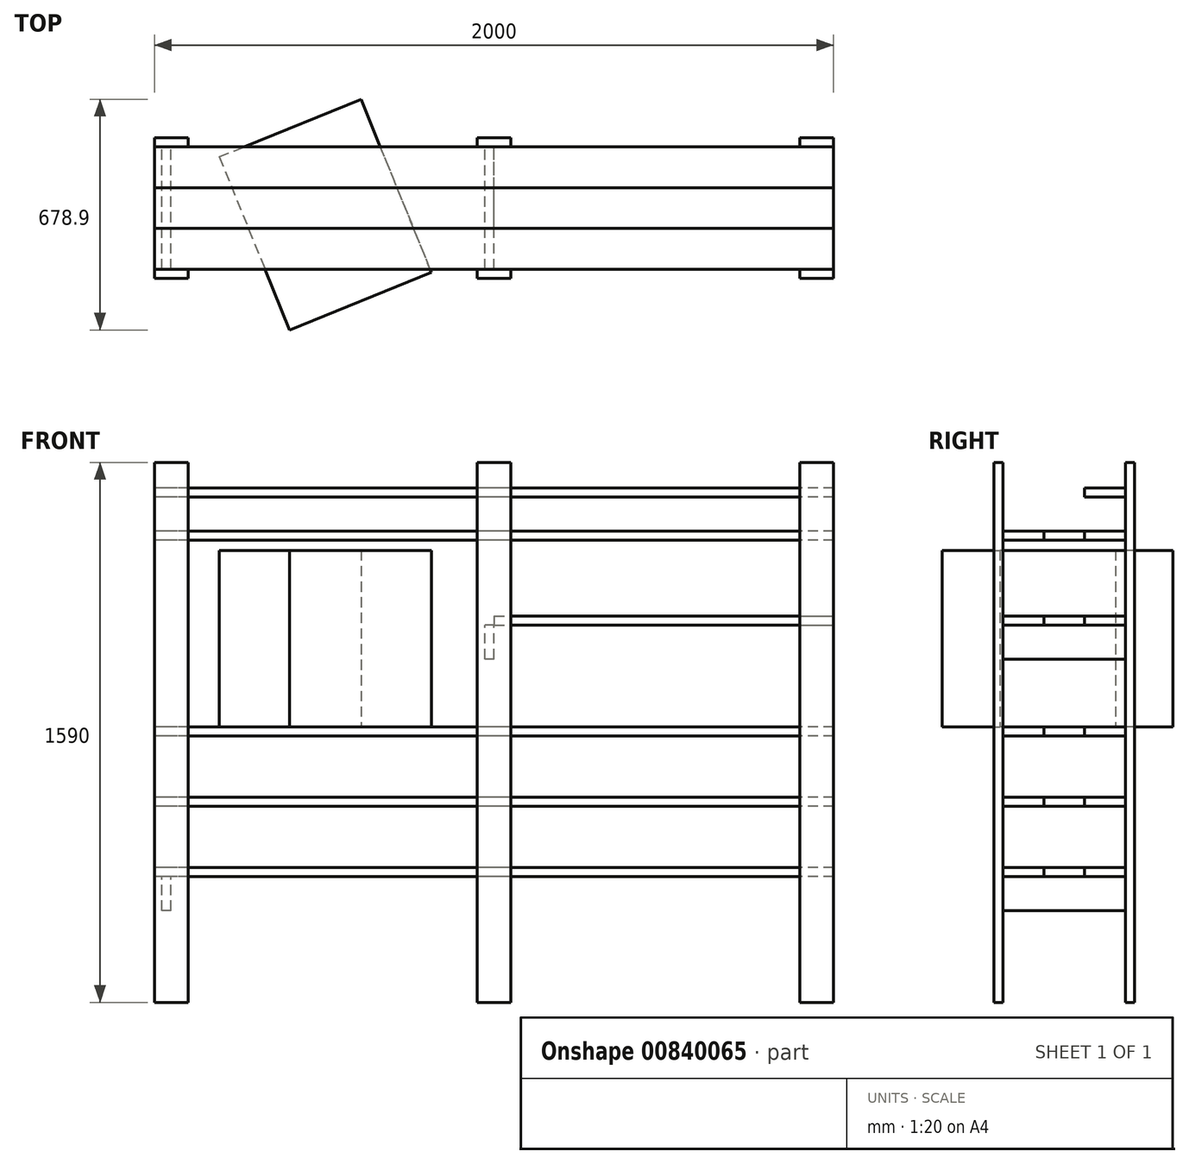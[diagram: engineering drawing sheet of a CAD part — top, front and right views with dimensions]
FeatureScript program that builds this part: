
annotation { "Feature Type Name" : "Feature", "Feature Type Description" : "" }
export const myFeature = defineFeature(function(context is Context, id is Id, definition is map)
    precondition{}
    {
        {
            var Q0;
            Q0=qCreatedBy(makeId("Top.planeOp"),FACE);
            var sketch = newSketch(context, id + "F0", { "sketchPlane" : qUnion([Q0])});
            skLineSegment(sketch, "E0.bottom", {"start": v(-127.38, 360.28) * mm, "end": v(-27.38, 360.28) * mm});
            skLineSegment(sketch, "E0.top", {"start": v(-127.38, 333.28) * mm, "end": v(-27.38, 333.28) * mm});
            skLineSegment(sketch, "E0.left", {"start": v(-127.38, 360.28) * mm, "end": v(-127.38, 333.28) * mm});
            skLineSegment(sketch, "E0.right", {"start": v(-27.38, 360.28) * mm, "end": v(-27.38, 333.28) * mm});
            skLineSegment(sketch, "E1.bottom", {"start": v(-127.38, -26.72) * mm, "end": v(-27.38, -26.72) * mm});
            skLineSegment(sketch, "E1.top", {"start": v(-127.38, -53.72) * mm, "end": v(-27.38, -53.72) * mm});
            skLineSegment(sketch, "E1.left", {"start": v(-127.38, -26.72) * mm, "end": v(-127.38, -53.72) * mm});
            skLineSegment(sketch, "E1.right", {"start": v(-27.38, -26.72) * mm, "end": v(-27.38, -53.72) * mm});
            skLineSegment(sketch, "E2.bottom", {"start": v(822.62, 360.28) * mm, "end": v(922.62, 360.28) * mm});
            skLineSegment(sketch, "E2.top", {"start": v(822.62, 333.28) * mm, "end": v(922.62, 333.28) * mm});
            skLineSegment(sketch, "E2.left", {"start": v(822.62, 360.28) * mm, "end": v(822.62, 333.28) * mm});
            skLineSegment(sketch, "E2.right", {"start": v(922.62, 360.28) * mm, "end": v(922.62, 333.28) * mm});
            skLineSegment(sketch, "E3.bottom", {"start": v(822.62, -26.72) * mm, "end": v(922.62, -26.72) * mm});
            skLineSegment(sketch, "E3.top", {"start": v(822.62, -53.72) * mm, "end": v(922.62, -53.72) * mm});
            skLineSegment(sketch, "E3.left", {"start": v(822.62, -26.72) * mm, "end": v(822.62, -53.72) * mm});
            skLineSegment(sketch, "E3.right", {"start": v(922.62, -26.72) * mm, "end": v(922.62, -53.72) * mm});
            skLineSegment(sketch, "E4.bottom", {"start": v(1772.62, 360.28) * mm, "end": v(1872.62, 360.28) * mm});
            skLineSegment(sketch, "E4.top", {"start": v(1772.62, 333.28) * mm, "end": v(1872.62, 333.28) * mm});
            skLineSegment(sketch, "E4.left", {"start": v(1772.62, 360.28) * mm, "end": v(1772.62, 333.28) * mm});
            skLineSegment(sketch, "E4.right", {"start": v(1872.62, 360.28) * mm, "end": v(1872.62, 333.28) * mm});
            skLineSegment(sketch, "E5.bottom", {"start": v(1772.62, -26.72) * mm, "end": v(1872.62, -26.72) * mm});
            skLineSegment(sketch, "E5.top", {"start": v(1772.62, -53.72) * mm, "end": v(1872.62, -53.72) * mm});
            skLineSegment(sketch, "E5.left", {"start": v(1772.62, -26.72) * mm, "end": v(1772.62, -53.72) * mm});
            skLineSegment(sketch, "E5.right", {"start": v(1872.62, -26.72) * mm, "end": v(1872.62, -53.72) * mm});
            skLineSegment(sketch, "E6", {"start": v(-127.38, 507.16) * mm, "end": v(1872.62, 507.16) * mm, "construction": true});
            skLineSegment(sketch, "E7", {"start": v(872.62, 507.16) * mm, "end": v(872.62, -137.02) * mm, "construction": true});
            skPoint(sketch, "E8", {"position": v(872.62, 360.28) * mm});
            skSolve(sketch);
        }
        {
            var Q0;
            Q0=makeQuery(id+"F0.imprint","IMPRINT",FACE,{"disambiguationData":[TD([[makeQuery(id+"F0.imprint","IMPRINT",EDGE,{"derivedFrom":sQuery(id+"F0.wireOp",EDGE,"E0.bottom")}),-1.0]])]});
            extrude(context, id + "F1", {"entities" : qUnion([Q0]), "depth" : 1590 * mm, "offsetDistance" : 25 * mm});
        }
        {
            var Q0;
            Q0 = qSketchRegion(id + "F0", true);
            var Q1;
            Q1=sQuery(id+"F0.wireOp",EDGE,"E1.right");
            var Q2;
            Q2=sQuery(id+"F0.wireOp",EDGE,"E1.bottom");
            var Q3;
            Q3=sQuery(id+"F0.wireOp",EDGE,"E1.left");
            var Q4;
            Q4=sQuery(id+"F0.wireOp",EDGE,"E1.top");
            extrude(context, id + "F2", {"entities" : qUnion([Q0]), "operationType" : NewBodyOperationType.ADD, "surfaceEntities" : qUnion([Q1, Q2, Q3, Q4]), "depth" : 1590 * mm, "offsetDistance" : 25 * mm});
        }
        {
            var Q0;
            Q0=makeQuery(id+"F2.opExtrude","SWEPT_FACE",FACE,{"disambiguationData":[OSD([sQuery(id+"F0.wireOp",EDGE,"E1.left")])]});
            var sketch = newSketch(context, id + "F3", { "sketchPlane" : qUnion([Q0])});
            skLineSegment(sketch, "E9.0", {"start": v(-333.28, 1590) * mm, "end": v(-333.28, 0) * mm});
            skLineSegment(sketch, "E10.bottom", {"start": v(26.72, 397) * mm, "end": v(-93.28, 397) * mm});
            skLineSegment(sketch, "E10.top", {"start": v(26.72, 370) * mm, "end": v(-93.28, 370) * mm});
            skLineSegment(sketch, "E10.left", {"start": v(26.72, 397) * mm, "end": v(26.72, 370) * mm});
            skLineSegment(sketch, "E10.right", {"start": v(-93.28, 397) * mm, "end": v(-93.28, 370) * mm});
            skLineSegment(sketch, "E11.bottom", {"start": v(-93.28, 397) * mm, "end": v(-213.28, 397) * mm});
            skLineSegment(sketch, "E11.top", {"start": v(-93.28, 370) * mm, "end": v(-213.28, 370) * mm});
            skLineSegment(sketch, "E11.right", {"start": v(-213.28, 397) * mm, "end": v(-213.28, 370) * mm});
            skLineSegment(sketch, "E12.bottom", {"start": v(-213.28, 397) * mm, "end": v(-333.28, 397) * mm});
            skLineSegment(sketch, "E12.top", {"start": v(-213.28, 370) * mm, "end": v(-333.28, 370) * mm});
            skLineSegment(sketch, "E12.right", {"start": v(-333.28, 397) * mm, "end": v(-333.28, 370) * mm});
            skLineSegment(sketch, "E13.bottom", {"start": v(26.72, 604) * mm, "end": v(-93.28, 604) * mm});
            skLineSegment(sketch, "E13.top", {"start": v(26.72, 577) * mm, "end": v(-93.28, 577) * mm});
            skLineSegment(sketch, "E13.left", {"start": v(26.72, 604) * mm, "end": v(26.72, 577) * mm});
            skLineSegment(sketch, "E13.right", {"start": v(-93.28, 604) * mm, "end": v(-93.28, 577) * mm});
            skLineSegment(sketch, "E14.bottom", {"start": v(-93.28, 604) * mm, "end": v(-213.28, 604) * mm});
            skLineSegment(sketch, "E14.top", {"start": v(-93.28, 577) * mm, "end": v(-213.28, 577) * mm});
            skLineSegment(sketch, "E14.right", {"start": v(-213.28, 604) * mm, "end": v(-213.28, 577) * mm});
            skLineSegment(sketch, "E15.bottom", {"start": v(-213.28, 604) * mm, "end": v(-333.28, 604) * mm});
            skLineSegment(sketch, "E15.top", {"start": v(-213.28, 577) * mm, "end": v(-333.28, 577) * mm});
            skLineSegment(sketch, "E15.right", {"start": v(-333.28, 604) * mm, "end": v(-333.28, 577) * mm});
            skLineSegment(sketch, "E16.bottom", {"start": v(26.72, 811) * mm, "end": v(-93.28, 811) * mm});
            skLineSegment(sketch, "E16.top", {"start": v(26.72, 784) * mm, "end": v(-93.28, 784) * mm});
            skLineSegment(sketch, "E16.left", {"start": v(26.72, 811) * mm, "end": v(26.72, 784) * mm});
            skLineSegment(sketch, "E16.right", {"start": v(-93.28, 811) * mm, "end": v(-93.28, 784) * mm});
            skLineSegment(sketch, "E17.bottom", {"start": v(-93.28, 811) * mm, "end": v(-213.28, 811) * mm});
            skLineSegment(sketch, "E17.top", {"start": v(-93.28, 784) * mm, "end": v(-213.28, 784) * mm});
            skLineSegment(sketch, "E17.right", {"start": v(-213.28, 811) * mm, "end": v(-213.28, 784) * mm});
            skLineSegment(sketch, "E18.bottom", {"start": v(-213.28, 811) * mm, "end": v(-333.28, 811) * mm});
            skLineSegment(sketch, "E18.top", {"start": v(-213.28, 784) * mm, "end": v(-333.28, 784) * mm});
            skLineSegment(sketch, "E18.right", {"start": v(-333.28, 811) * mm, "end": v(-333.28, 784) * mm});
            skLineSegment(sketch, "E19.bottom", {"start": v(26.72, 1388) * mm, "end": v(-93.28, 1388) * mm});
            skLineSegment(sketch, "E19.top", {"start": v(26.72, 1361) * mm, "end": v(-93.28, 1361) * mm});
            skLineSegment(sketch, "E19.left", {"start": v(26.72, 1388) * mm, "end": v(26.72, 1361) * mm});
            skLineSegment(sketch, "E19.right", {"start": v(-93.28, 1388) * mm, "end": v(-93.28, 1361) * mm});
            skLineSegment(sketch, "E20.bottom", {"start": v(-93.28, 1388) * mm, "end": v(-213.28, 1388) * mm});
            skLineSegment(sketch, "E20.top", {"start": v(-93.28, 1361) * mm, "end": v(-213.28, 1361) * mm});
            skLineSegment(sketch, "E20.right", {"start": v(-213.28, 1388) * mm, "end": v(-213.28, 1361) * mm});
            skLineSegment(sketch, "E21.bottom", {"start": v(-213.28, 1388) * mm, "end": v(-333.28, 1388) * mm});
            skLineSegment(sketch, "E21.top", {"start": v(-213.28, 1361) * mm, "end": v(-333.28, 1361) * mm});
            skLineSegment(sketch, "E21.right", {"start": v(-333.28, 1388) * mm, "end": v(-333.28, 1361) * mm});
            skLineSegment(sketch, "E22.bottom", {"start": v(-333.28, 1515) * mm, "end": v(-213.28, 1515) * mm});
            skLineSegment(sketch, "E22.top", {"start": v(-333.28, 1488) * mm, "end": v(-213.28, 1488) * mm});
            skLineSegment(sketch, "E22.left", {"start": v(-333.28, 1515) * mm, "end": v(-333.28, 1488) * mm});
            skLineSegment(sketch, "E22.right", {"start": v(-213.28, 1515) * mm, "end": v(-213.28, 1488) * mm});
            skSolve(sketch);
        }
        {
            var Q0;
            Q0=makeQuery(id+"F3.imprint","IMPRINT",FACE,{"disambiguationData":[TD([[makeQuery(id+"F3.imprint","IMPRINT",EDGE,{"derivedFrom":sQuery(id+"F3.wireOp",EDGE,"E12.bottom")}),1.0]])]});
            var Q1;
            Q1=makeQuery(id+"F3.imprint","IMPRINT",FACE,{"disambiguationData":[TD([[makeQuery(id+"F3.imprint","IMPRINT",EDGE,{"derivedFrom":sQuery(id+"F3.wireOp",EDGE,"E10.bottom")}),1.0]])]});
            extrude(context, id + "F4", {"entities" : qUnion([Q0, Q1]), "oppositeDirection" : true, "depth" : 2000 * mm, "offsetDistance" : 25 * mm});
        }
        {
            var Q0;
            Q0=makeQuery(id+"F3.imprint","IMPRINT",FACE,{"disambiguationData":[TD([[makeQuery(id+"F3.imprint","IMPRINT",EDGE,{"derivedFrom":sQuery(id+"F3.wireOp",EDGE,"E21.bottom")}),1.0]])]});
            var Q1;
            Q1=makeQuery(id+"F3.imprint","IMPRINT",FACE,{"disambiguationData":[TD([[makeQuery(id+"F3.imprint","IMPRINT",EDGE,{"derivedFrom":sQuery(id+"F3.wireOp",EDGE,"E19.bottom")}),1.0]])]});
            var Q2;
            Q2=makeQuery(id+"F3.imprint","IMPRINT",FACE,{"disambiguationData":[TD([[makeQuery(id+"F3.imprint","IMPRINT",EDGE,{"derivedFrom":sQuery(id+"F3.wireOp",EDGE,"E16.bottom")}),1.0]])]});
            var Q3;
            Q3=makeQuery(id+"F3.imprint","IMPRINT",FACE,{"disambiguationData":[TD([[makeQuery(id+"F3.imprint","IMPRINT",EDGE,{"derivedFrom":sQuery(id+"F3.wireOp",EDGE,"E18.bottom")}),1.0]])]});
            var Q4;
            Q4=makeQuery(id+"F3.imprint","IMPRINT",FACE,{"disambiguationData":[TD([[makeQuery(id+"F3.imprint","IMPRINT",EDGE,{"derivedFrom":sQuery(id+"F3.wireOp",EDGE,"E15.bottom")}),1.0]])]});
            var Q5;
            Q5=makeQuery(id+"F3.imprint","IMPRINT",FACE,{"disambiguationData":[TD([[makeQuery(id+"F3.imprint","IMPRINT",EDGE,{"derivedFrom":sQuery(id+"F3.wireOp",EDGE,"E13.bottom")}),1.0]])]});
            extrude(context, id + "F5", {"entities" : qUnion([Q0, Q1, Q2, Q3, Q4, Q5]), "oppositeDirection" : true, "depth" : 2000 * mm, "offsetDistance" : 25 * mm});
        }
        {
            var Q0;
            Q0=makeQuery(id+"F3.imprint","IMPRINT",FACE,{"disambiguationData":[TD([[makeQuery(id+"F3.imprint","IMPRINT",EDGE,{"derivedFrom":sQuery(id+"F3.wireOp",EDGE,"E20.bottom")}),1.0]])]});
            var Q1;
            Q1=makeQuery(id+"F3.imprint","IMPRINT",FACE,{"disambiguationData":[TD([[makeQuery(id+"F3.imprint","IMPRINT",EDGE,{"derivedFrom":sQuery(id+"F3.wireOp",EDGE,"E17.bottom")}),1.0]])]});
            var Q2;
            Q2=makeQuery(id+"F3.imprint","IMPRINT",FACE,{"disambiguationData":[TD([[makeQuery(id+"F3.imprint","IMPRINT",EDGE,{"derivedFrom":sQuery(id+"F3.wireOp",EDGE,"E14.bottom")}),1.0]])]});
            var Q3;
            Q3=makeQuery(id+"F3.imprint","IMPRINT",FACE,{"disambiguationData":[TD([[makeQuery(id+"F3.imprint","IMPRINT",EDGE,{"derivedFrom":sQuery(id+"F3.wireOp",EDGE,"E11.bottom")}),1.0]])]});
            extrude(context, id + "F6", {"entities" : qUnion([Q0, Q1, Q2, Q3]), "oppositeDirection" : true, "depth" : 2000 * mm, "offsetDistance" : 25 * mm});
        }
        {
            var Q0;
            Q0=makeQuery(id+"F5.opExtrude","SWEPT_FACE",FACE,{"disambiguationData":[OSD([sQuery(id+"F3.wireOp",EDGE,"E16.bottom")])]});
            var sketch = newSketch(context, id + "F7", { "sketchPlane" : qUnion([Q0])});
            skLineSegment(sketch, "E23.bottom", {"start": v(64.1, 303.8) * mm, "end": v(481.04, 473.12) * mm});
            skLineSegment(sketch, "E23.top", {"start": v(271.05, -205.78) * mm, "end": v(687.98, -36.47) * mm});
            skLineSegment(sketch, "E23.left", {"start": v(64.1, 303.8) * mm, "end": v(271.05, -205.78) * mm});
            skLineSegment(sketch, "E23.right", {"start": v(481.04, 473.12) * mm, "end": v(687.98, -36.47) * mm});
            skSolve(sketch);
        }
        {
            var Q0;
            Q0 = qSketchRegion(id + "F7", true);
            extrude(context, id + "F8", {"entities" : qUnion([Q0]), "depth" : 520 * mm, "offsetDistance" : 25 * mm});
        }
        {
            var Q0;
            Q0=makeQuery(id+"F2.opExtrude","SWEPT_FACE",FACE,{"disambiguationData":[OSD([sQuery(id+"F0.wireOp",EDGE,"E5.right")])]});
            var sketch = newSketch(context, id + "F9", { "sketchPlane" : qUnion([Q0])});
            skLineSegment(sketch, "E24.bottom", {"start": v(-26.72, 1138) * mm, "end": v(93.28, 1138) * mm});
            skLineSegment(sketch, "E24.top", {"start": v(-26.72, 1111) * mm, "end": v(93.28, 1111) * mm});
            skLineSegment(sketch, "E24.left", {"start": v(-26.72, 1138) * mm, "end": v(-26.72, 1111) * mm});
            skLineSegment(sketch, "E24.right", {"start": v(93.28, 1138) * mm, "end": v(93.28, 1111) * mm});
            skLineSegment(sketch, "E25.0.0", {"start": v(-26.72, 811) * mm, "end": v(-26.72, 784) * mm});
            skLineSegment(sketch, "E25.0.1", {"start": v(-26.72, 784) * mm, "end": v(93.28, 784) * mm});
            skLineSegment(sketch, "E25.0.2", {"start": v(93.28, 784) * mm, "end": v(93.28, 811) * mm});
            skLineSegment(sketch, "E25.0.3", {"start": v(93.28, 811) * mm, "end": v(-26.72, 811) * mm});
            skLineSegment(sketch, "E26.0.2", {"start": v(213.28, 811) * mm, "end": v(93.28, 811) * mm});
            skLineSegment(sketch, "E26.0.3", {"start": v(93.28, 811) * mm, "end": v(93.28, 784) * mm});
            skLineSegment(sketch, "E27.0.0", {"start": v(333.28, 811) * mm, "end": v(213.28, 811) * mm});
            skLineSegment(sketch, "E28.bottom", {"start": v(93.28, 1138) * mm, "end": v(213.28, 1138) * mm});
            skLineSegment(sketch, "E28.top", {"start": v(93.28, 1111) * mm, "end": v(213.28, 1111) * mm});
            skLineSegment(sketch, "E28.right", {"start": v(213.28, 1138) * mm, "end": v(213.28, 1111) * mm});
            skLineSegment(sketch, "E29.bottom", {"start": v(213.28, 1138) * mm, "end": v(333.28, 1138) * mm});
            skLineSegment(sketch, "E29.top", {"start": v(213.28, 1111) * mm, "end": v(333.28, 1111) * mm});
            skLineSegment(sketch, "E29.right", {"start": v(333.28, 1138) * mm, "end": v(333.28, 1111) * mm});
            skSolve(sketch);
        }
        {
            var Q0;
            Q0=makeQuery(id+"F9.imprint","IMPRINT",FACE,{"disambiguationData":[TD([[makeQuery(id+"F9.imprint","IMPRINT",EDGE,{"derivedFrom":sQuery(id+"F9.wireOp",EDGE,"E24.bottom")}),-1.0]])]});
            var Q1;
            Q1=makeQuery(id+"F9.imprint","IMPRINT",FACE,{"disambiguationData":[TD([[makeQuery(id+"F9.imprint","IMPRINT",EDGE,{"derivedFrom":sQuery(id+"F9.wireOp",EDGE,"E29.bottom")}),-1.0]])]});
            extrude(context, id + "F10", {"entities" : qUnion([Q0, Q1]), "oppositeDirection" : true, "depth" : 1000 * mm, "offsetDistance" : 25 * mm});
        }
        {
            var Q0;
            Q0=makeQuery(id+"F9.imprint","IMPRINT",FACE,{"disambiguationData":[TD([[makeQuery(id+"F9.imprint","IMPRINT",EDGE,{"derivedFrom":sQuery(id+"F9.wireOp",EDGE,"E28.bottom")}),-1.0]])]});
            extrude(context, id + "F11", {"entities" : qUnion([Q0]), "oppositeDirection" : true, "depth" : 1000 * mm, "offsetDistance" : 25 * mm});
        }
        {
            var Q0;
            Q0=makeQuery(id+"F3.imprint","IMPRINT",FACE,{"disambiguationData":[TD([[makeQuery(id+"F3.imprint","IMPRINT",EDGE,{"derivedFrom":sQuery(id+"F3.wireOp",EDGE,"E22.bottom")}),-1.0]])]});
            extrude(context, id + "F12", {"entities" : qUnion([Q0]), "oppositeDirection" : true, "depth" : 2000 * mm, "offsetDistance" : 25 * mm});
        }
        {
            var Q0;
            Q0=makeQuery(id+"F2.opExtrude","SWEPT_FACE",FACE,{"disambiguationData":[OSD([sQuery(id+"F0.wireOp",EDGE,"E4.top")])]});
            var sketch = newSketch(context, id + "F13", { "sketchPlane" : qUnion([Q0])});
            skLineSegment(sketch, "E30.0", {"start": v(1872.62, 784) * mm, "end": v(-127.38, 784) * mm});
            skLineSegment(sketch, "E31.0", {"start": v(1772.62, 1590) * mm, "end": v(1772.62, 0) * mm});
            skPoint(sketch, "E32.firstSnap0", {"position": v(1772.62, 795) * mm});
            skLineSegment(sketch, "E32.bottom", {"start": v(-105.73, 784) * mm, "end": v(-78.73, 784) * mm});
            skLineSegment(sketch, "E32.top", {"start": v(-105.73, 684) * mm, "end": v(-78.73, 684) * mm});
            skLineSegment(sketch, "E32.left", {"start": v(-105.73, 784) * mm, "end": v(-105.73, 684) * mm});
            skLineSegment(sketch, "E32.right", {"start": v(-78.73, 784) * mm, "end": v(-78.73, 684) * mm});
            skPoint(sketch, "E33.0", {"position": v(1872.62, 797.5) * mm});
            skLineSegment(sketch, "E34.0.0", {"start": v(1872.62, 1111) * mm, "end": v(1872.62, 1138) * mm});
            skLineSegment(sketch, "E34.0.1", {"start": v(1872.62, 1138) * mm, "end": v(872.62, 1138) * mm});
            skLineSegment(sketch, "E34.0.2", {"start": v(872.62, 1138) * mm, "end": v(872.62, 1111) * mm});
            skLineSegment(sketch, "E34.0.3", {"start": v(872.62, 1111) * mm, "end": v(1872.62, 1111) * mm});
            skLineSegment(sketch, "E35.bottom", {"start": v(-105.73, 1111) * mm, "end": v(-78.73, 1111) * mm});
            skLineSegment(sketch, "E35.top", {"start": v(-105.73, 1011) * mm, "end": v(-78.73, 1011) * mm});
            skLineSegment(sketch, "E35.left", {"start": v(-105.73, 1111) * mm, "end": v(-105.73, 1011) * mm});
            skLineSegment(sketch, "E35.right", {"start": v(-78.73, 1111) * mm, "end": v(-78.73, 1011) * mm});
            skPoint(sketch, "E36.firstSnap0", {"position": v(-105.73, 881.34) * mm});
            skLineSegment(sketch, "E36.bottom", {"start": v(-105.73, 370) * mm, "end": v(-78.73, 370) * mm});
            skLineSegment(sketch, "E36.top", {"start": v(-105.73, 270) * mm, "end": v(-78.73, 270) * mm});
            skLineSegment(sketch, "E36.left", {"start": v(-105.73, 370) * mm, "end": v(-105.73, 270) * mm});
            skLineSegment(sketch, "E36.right", {"start": v(-78.73, 370) * mm, "end": v(-78.73, 270) * mm});
            skLineSegment(sketch, "E37.0", {"start": v(1872.62, 370) * mm, "end": v(-127.38, 370) * mm});
            skLineSegment(sketch, "E37.2", {"start": v(1872.62, 1361) * mm, "end": v(-127.38, 1361) * mm});
            skLineSegment(sketch, "E37.3", {"start": v(1872.62, 1488) * mm, "end": v(-127.38, 1488) * mm});
            skLineSegment(sketch, "E37.4", {"start": v(822.62, 1590) * mm, "end": v(822.62, 0) * mm});
            skLineSegment(sketch, "E37.6", {"start": v(1872.62, 577) * mm, "end": v(-127.38, 577) * mm});
            skLineSegment(sketch, "E37.7", {"start": v(-27.38, 1590) * mm, "end": v(-27.38, 0) * mm});
            skLineSegment(sketch, "E38.bottom", {"start": v(-105.73, 1361) * mm, "end": v(-78.73, 1361) * mm});
            skLineSegment(sketch, "E38.top", {"start": v(-105.73, 1261) * mm, "end": v(-78.73, 1261) * mm});
            skLineSegment(sketch, "E38.left", {"start": v(-78.73, 1361) * mm, "end": v(-78.73, 1261) * mm});
            skLineSegment(sketch, "E38.right", {"start": v(-105.73, 1361) * mm, "end": v(-105.73, 1261) * mm});
            skLineSegment(sketch, "E39.bottom", {"start": v(-105.73, 1488) * mm, "end": v(-78.73, 1488) * mm});
            skLineSegment(sketch, "E39.top", {"start": v(-105.73, 1388) * mm, "end": v(-78.73, 1388) * mm});
            skLineSegment(sketch, "E39.left", {"start": v(-105.73, 1488) * mm, "end": v(-105.73, 1388) * mm});
            skLineSegment(sketch, "E39.right", {"start": v(-78.73, 1488) * mm, "end": v(-78.73, 1388) * mm});
            skLineSegment(sketch, "E40.bottom", {"start": v(845.62, 784) * mm, "end": v(872.62, 784) * mm});
            skLineSegment(sketch, "E40.top", {"start": v(845.62, 684) * mm, "end": v(872.62, 684) * mm});
            skLineSegment(sketch, "E40.left", {"start": v(845.62, 784) * mm, "end": v(845.62, 684) * mm});
            skLineSegment(sketch, "E40.right", {"start": v(872.62, 784) * mm, "end": v(872.62, 684) * mm});
            skLineSegment(sketch, "E41.bottom", {"start": v(845.62, 1111) * mm, "end": v(872.62, 1111) * mm});
            skLineSegment(sketch, "E41.top", {"start": v(845.62, 1011) * mm, "end": v(872.62, 1011) * mm});
            skLineSegment(sketch, "E41.left", {"start": v(845.62, 1111) * mm, "end": v(845.62, 1011) * mm});
            skLineSegment(sketch, "E41.right", {"start": v(872.62, 1111) * mm, "end": v(872.62, 1011) * mm});
            skPoint(sketch, "E42.firstSnap0", {"position": v(845.62, 854) * mm});
            skLineSegment(sketch, "E42.bottom", {"start": v(845.62, 370) * mm, "end": v(872.62, 370) * mm});
            skLineSegment(sketch, "E42.top", {"start": v(845.62, 270) * mm, "end": v(872.62, 270) * mm});
            skLineSegment(sketch, "E42.left", {"start": v(845.62, 370) * mm, "end": v(845.62, 270) * mm});
            skLineSegment(sketch, "E42.right", {"start": v(872.62, 370) * mm, "end": v(872.62, 270) * mm});
            skLineSegment(sketch, "E43.bottom", {"start": v(845.62, 1361) * mm, "end": v(872.62, 1361) * mm});
            skLineSegment(sketch, "E43.top", {"start": v(845.62, 1261) * mm, "end": v(872.62, 1261) * mm});
            skLineSegment(sketch, "E43.left", {"start": v(872.62, 1361) * mm, "end": v(872.62, 1261) * mm});
            skLineSegment(sketch, "E43.right", {"start": v(845.62, 1361) * mm, "end": v(845.62, 1261) * mm});
            skLineSegment(sketch, "E44.bottom", {"start": v(845.62, 1488) * mm, "end": v(872.62, 1488) * mm});
            skLineSegment(sketch, "E44.top", {"start": v(845.62, 1388) * mm, "end": v(872.62, 1388) * mm});
            skLineSegment(sketch, "E44.left", {"start": v(845.62, 1488) * mm, "end": v(845.62, 1388) * mm});
            skLineSegment(sketch, "E44.right", {"start": v(872.62, 1488) * mm, "end": v(872.62, 1388) * mm});
            skLineSegment(sketch, "E45.bottom", {"start": v(-105.73, 577) * mm, "end": v(-78.73, 577) * mm});
            skLineSegment(sketch, "E45.top", {"start": v(-105.73, 477) * mm, "end": v(-78.73, 477) * mm});
            skLineSegment(sketch, "E45.left", {"start": v(-105.73, 577) * mm, "end": v(-105.73, 477) * mm});
            skLineSegment(sketch, "E45.right", {"start": v(-78.73, 577) * mm, "end": v(-78.73, 477) * mm});
            skLineSegment(sketch, "E46.bottom", {"start": v(845.62, 577) * mm, "end": v(872.62, 577) * mm});
            skLineSegment(sketch, "E46.top", {"start": v(845.62, 477) * mm, "end": v(872.62, 477) * mm});
            skLineSegment(sketch, "E46.left", {"start": v(845.62, 577) * mm, "end": v(845.62, 477) * mm});
            skLineSegment(sketch, "E46.right", {"start": v(872.62, 577) * mm, "end": v(872.62, 477) * mm});
            skPoint(sketch, "E47.firstSnap0", {"position": v(1863.16, 759.3) * mm});
            skLineSegment(sketch, "E47.bottom", {"start": v(1801.68, 784) * mm, "end": v(1828.68, 784) * mm});
            skLineSegment(sketch, "E47.top", {"start": v(1801.68, 684) * mm, "end": v(1828.68, 684) * mm});
            skLineSegment(sketch, "E47.left", {"start": v(1801.68, 784) * mm, "end": v(1801.68, 684) * mm});
            skLineSegment(sketch, "E47.right", {"start": v(1828.68, 784) * mm, "end": v(1828.68, 684) * mm});
            skPoint(sketch, "E48.0", {"position": v(1763.16, 761.8) * mm});
            skLineSegment(sketch, "E49.0.0", {"start": v(1763.16, 1075.3) * mm, "end": v(1763.16, 1102.3) * mm});
            skPoint(sketch, "E50.firstSnap0", {"position": v(1801.68, 863.25) * mm});
            skLineSegment(sketch, "E50.bottom", {"start": v(1801.68, 370) * mm, "end": v(1828.68, 370) * mm});
            skLineSegment(sketch, "E50.top", {"start": v(1801.68, 270) * mm, "end": v(1828.68, 270) * mm});
            skLineSegment(sketch, "E50.left", {"start": v(1801.68, 370) * mm, "end": v(1801.68, 270) * mm});
            skLineSegment(sketch, "E50.right", {"start": v(1828.68, 370) * mm, "end": v(1828.68, 270) * mm});
            skLineSegment(sketch, "E51.bottom", {"start": v(1801.68, 1361) * mm, "end": v(1828.68, 1361) * mm});
            skLineSegment(sketch, "E51.top", {"start": v(1801.68, 1261) * mm, "end": v(1828.68, 1261) * mm});
            skLineSegment(sketch, "E51.left", {"start": v(1828.68, 1361) * mm, "end": v(1828.68, 1261) * mm});
            skLineSegment(sketch, "E51.right", {"start": v(1801.68, 1361) * mm, "end": v(1801.68, 1261) * mm});
            skLineSegment(sketch, "E52.bottom", {"start": v(1801.68, 1488) * mm, "end": v(1828.68, 1488) * mm});
            skLineSegment(sketch, "E52.top", {"start": v(1801.68, 1388) * mm, "end": v(1828.68, 1388) * mm});
            skLineSegment(sketch, "E52.left", {"start": v(1801.68, 1488) * mm, "end": v(1801.68, 1388) * mm});
            skLineSegment(sketch, "E52.right", {"start": v(1828.68, 1488) * mm, "end": v(1828.68, 1388) * mm});
            skLineSegment(sketch, "E53.bottom", {"start": v(1801.68, 577) * mm, "end": v(1828.68, 577) * mm});
            skLineSegment(sketch, "E53.top", {"start": v(1801.68, 477) * mm, "end": v(1828.68, 477) * mm});
            skLineSegment(sketch, "E53.left", {"start": v(1801.68, 577) * mm, "end": v(1801.68, 477) * mm});
            skLineSegment(sketch, "E53.right", {"start": v(1828.68, 577) * mm, "end": v(1828.68, 477) * mm});
            skSolve(sketch);
        }
        {
            var Q0;
            Q0=makeQuery(id+"F13.imprint","IMPRINT",FACE,{"disambiguationData":[TD([[makeQuery(id+"F13.imprint","IMPRINT",EDGE,{"derivedFrom":sQuery(id+"F13.wireOp",EDGE,"E47.bottom")}),-1.0]])]});
            var Q1;
            Q1=makeQuery(id+"F13.imprint","IMPRINT",FACE,{"disambiguationData":[TD([[makeQuery(id+"F13.imprint","IMPRINT",EDGE,{"derivedFrom":sQuery(id+"F13.wireOp",EDGE,"E53.bottom")}),-1.0]])]});
            var Q2;
            Q2=makeQuery(id+"F13.imprint","IMPRINT",FACE,{"disambiguationData":[TD([[makeQuery(id+"F13.imprint","IMPRINT",EDGE,{"derivedFrom":sQuery(id+"F13.wireOp",EDGE,"E50.bottom")}),-1.0]])]});
            var Q3;
            Q3=makeQuery(id+"F13.imprint","IMPRINT",FACE,{"disambiguationData":[TD([[makeQuery(id+"F13.imprint","IMPRINT",EDGE,{"derivedFrom":sQuery(id+"F13.wireOp",EDGE,"E51.bottom")}),-1.0]])]});
            var Q4;
            Q4=makeQuery(id+"F13.imprint","IMPRINT",FACE,{"disambiguationData":[TD([[makeQuery(id+"F13.imprint","IMPRINT",EDGE,{"derivedFrom":sQuery(id+"F13.wireOp",EDGE,"E40.bottom")}),-1.0]])]});
            var Q5;
            Q5=makeQuery(id+"F13.imprint","IMPRINT",FACE,{"disambiguationData":[TD([[makeQuery(id+"F13.imprint","IMPRINT",EDGE,{"derivedFrom":sQuery(id+"F13.wireOp",EDGE,"E46.bottom")}),-1.0]])]});
            var Q6;
            Q6=makeQuery(id+"F13.imprint","IMPRINT",FACE,{"disambiguationData":[TD([[makeQuery(id+"F13.imprint","IMPRINT",EDGE,{"derivedFrom":sQuery(id+"F13.wireOp",EDGE,"E42.bottom")}),-1.0]])]});
            var Q7;
            Q7=makeQuery(id+"F13.imprint","IMPRINT",FACE,{"disambiguationData":[TD([[makeQuery(id+"F13.imprint","IMPRINT",EDGE,{"derivedFrom":sQuery(id+"F13.wireOp",EDGE,"E41.bottom")}),-1.0]])]});
            var Q8;
            Q8=makeQuery(id+"F13.imprint","IMPRINT",FACE,{"disambiguationData":[TD([[makeQuery(id+"F13.imprint","IMPRINT",EDGE,{"derivedFrom":sQuery(id+"F13.wireOp",EDGE,"E43.bottom")}),-1.0]])]});
            var Q9;
            Q9=makeQuery(id+"F13.imprint","IMPRINT",FACE,{"disambiguationData":[TD([[makeQuery(id+"F13.imprint","IMPRINT",EDGE,{"derivedFrom":sQuery(id+"F13.wireOp",EDGE,"E36.top")}),1.0]])]});
            var Q10;
            Q10=makeQuery(id+"F13.imprint","IMPRINT",FACE,{"disambiguationData":[TD([[makeQuery(id+"F13.imprint","IMPRINT",EDGE,{"derivedFrom":sQuery(id+"F13.wireOp",EDGE,"E45.bottom")}),-1.0]])]});
            var Q11;
            Q11=makeQuery(id+"F13.imprint","IMPRINT",FACE,{"disambiguationData":[TD([[makeQuery(id+"F13.imprint","IMPRINT",EDGE,{"derivedFrom":sQuery(id+"F13.wireOp",EDGE,"E32.bottom")}),-1.0]])]});
            var Q12;
            Q12=makeQuery(id+"F13.imprint","IMPRINT",FACE,{"disambiguationData":[TD([[makeQuery(id+"F13.imprint","IMPRINT",EDGE,{"derivedFrom":sQuery(id+"F13.wireOp",EDGE,"E52.bottom")}),-1.0]])]});
            var Q13;
            Q13=makeQuery(id+"F2.opExtrude","SWEPT_FACE",FACE,{"disambiguationData":[OSD([sQuery(id+"F0.wireOp",EDGE,"E5.bottom")])]});
            extrude(context, id + "F14", {"entities" : qUnion([Q0, Q1, Q2, Q3, Q4, Q5, Q6, Q7, Q8, Q9, Q10, Q11, Q12]), "endBound" : BoundingType.UP_TO_SURFACE, "depth" : 25 * mm, "endBoundEntityFace" : qUnion([Q13]), "offsetDistance" : 25 * mm});
        }
    });
